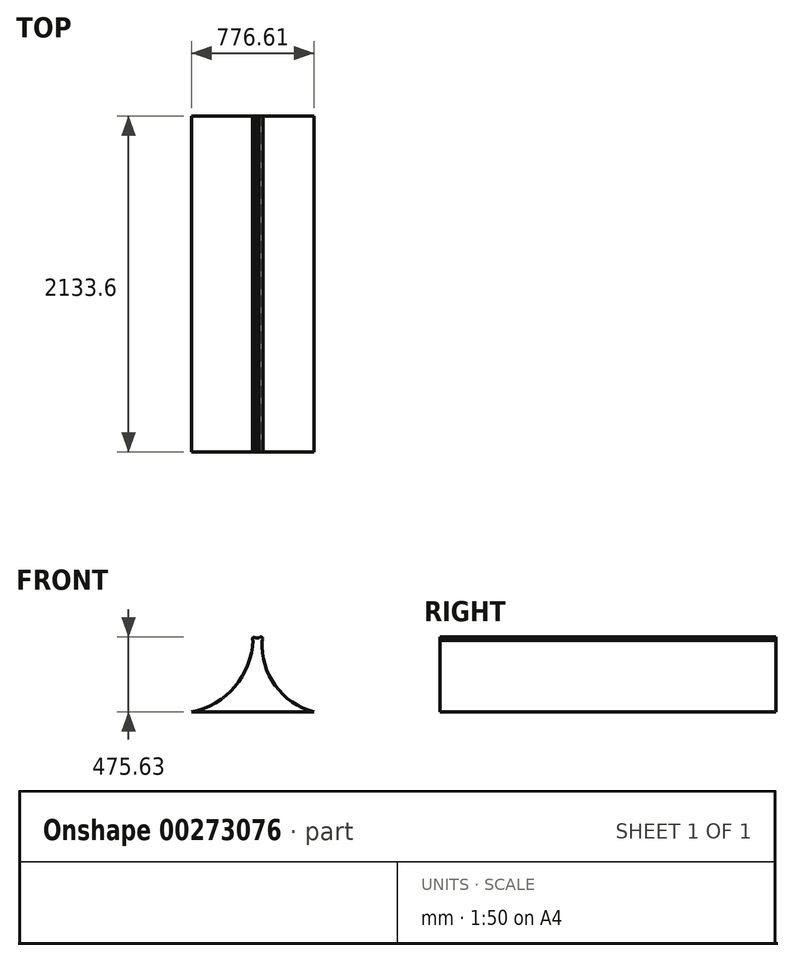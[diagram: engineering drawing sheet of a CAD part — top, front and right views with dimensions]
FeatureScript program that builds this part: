
annotation { "Feature Type Name" : "Feature", "Feature Type Description" : "" }
export const myFeature = defineFeature(function(context is Context, id is Id, definition is map)
    precondition{}
    {
        {
            var Q0;
            Q0=qCreatedBy(makeId("Front.planeOp"),FACE);
            var sketch = newSketch(context, id + "F0", { "sketchPlane" : qUnion([Q0])});
            skArc(sketch, "E0", {"start": v(-389.15, -227.6) * mm, "mid": v(-115.09, -68.75) * mm, "end": v(-0.27, 226.49) * mm});
            skLineSegment(sketch, "E1", {"start": v(15.74, 242.57) * mm, "end": v(40.12, 242.57) * mm});
            skArc(sketch, "E2", {"start": v(58.43, 224.67) * mm, "mid": v(141.32, -61.13) * mm, "end": v(387.46, -228.38) * mm});
            skLineSegment(sketch, "E3", {"start": v(-389.15, -227.6) * mm, "end": v(387.46, -228.38) * mm});
            skArc(sketch, "E4", {"start": v(15.74, 242.57) * mm, "mid": v(-0.17, 242.4) * mm, "end": v(-0.27, 226.49) * mm});
            skArc(sketch, "E5", {"start": v(58.43, 224.67) * mm, "mid": v(59, 243.59) * mm, "end": v(40.12, 242.57) * mm});
            skPoint(sketch, "E6.orphan", {"position": v(0, 242.57) * mm});
            skSolve(sketch);
        }
        {
            var Q0;
            Q0 = qSketchRegion(id + "F0", true);
            extrude(context, id + "F1", {"entities" : qUnion([Q0]), "depth" : 2133.6 * mm});
        }
    });
